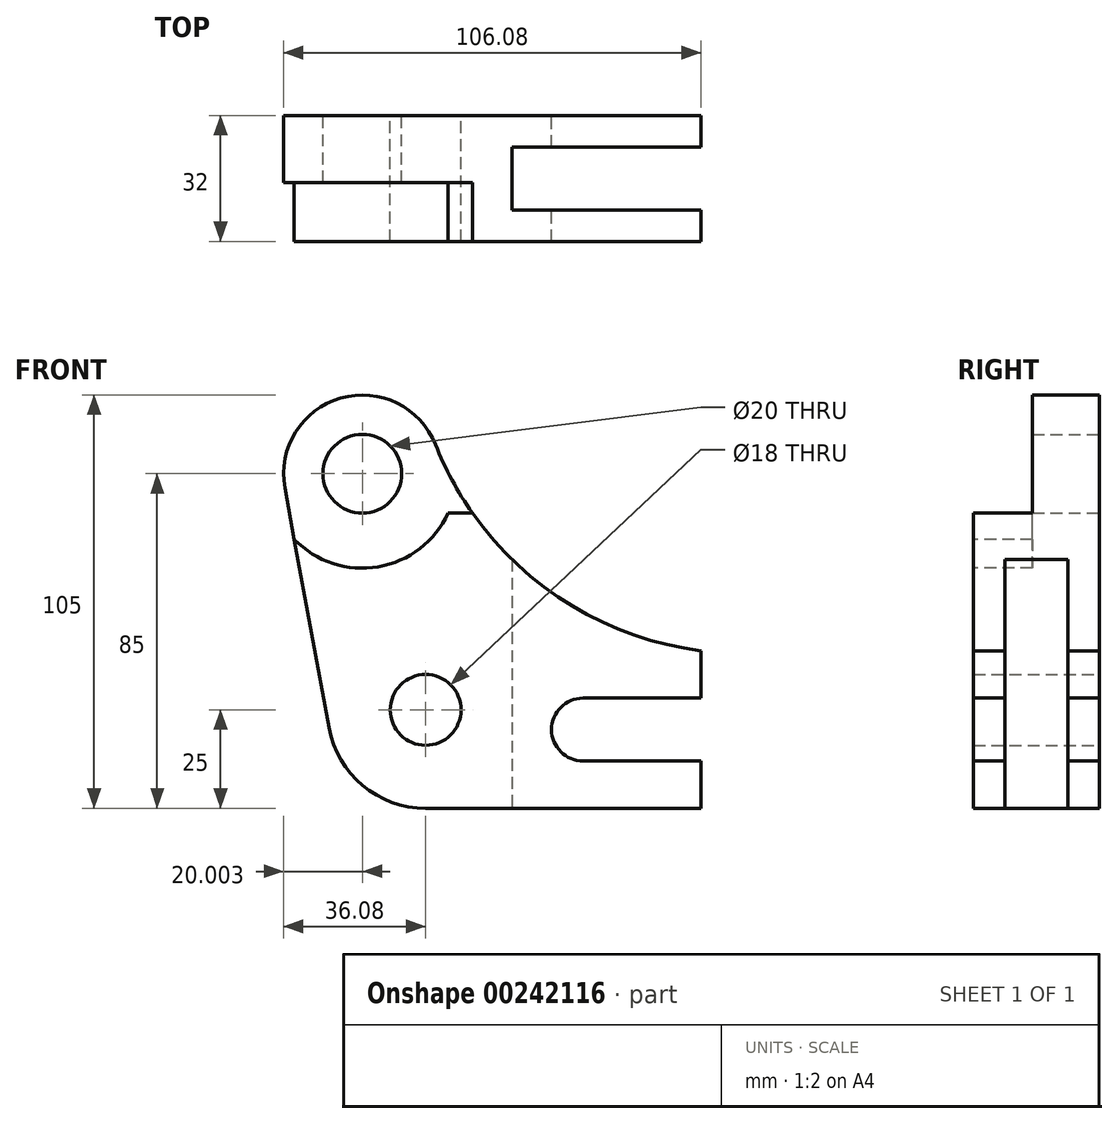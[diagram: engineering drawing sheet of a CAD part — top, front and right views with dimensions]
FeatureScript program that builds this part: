
annotation { "Feature Type Name" : "Feature", "Feature Type Description" : "" }
export const myFeature = defineFeature(function(context is Context, id is Id, definition is map)
    precondition{}
    {
        {
            var Q0;
            Q0=qCreatedBy(makeId("Front.planeOp"),FACE);
            var sketch = newSketch(context, id + "F0", { "sketchPlane" : qUnion([Q0])});
            skLineSegment(sketch, "E0", {"start": v(0, 0) * mm, "end": v(-70, 0) * mm});
            skLineSegment(sketch, "E1", {"start": v(-94.6, 20.5) * mm, "end": v(-105.75, 81.4) * mm});
            skLineSegment(sketch, "E2", {"start": v(0, 0) * mm, "end": v(0, 12) * mm});
            skLineSegment(sketch, "E3", {"start": v(0, 12) * mm, "end": v(-30, 12) * mm});
            skLineSegment(sketch, "E4", {"start": v(-30, 28) * mm, "end": v(0, 28) * mm});
            skLineSegment(sketch, "E5", {"start": v(0, 28) * mm, "end": v(0, 40) * mm});
            skArc(sketch, "E6", {"start": v(-30, 28) * mm, "mid": v(-38, 20) * mm, "end": v(-30, 12) * mm});
            skArc(sketch, "E7", {"start": v(-70, 0) * mm, "mid": v(-86, 5.8) * mm, "end": v(-94.6, 20.5) * mm});
            skArc(sketch, "E8", {"start": v(-67.48, 92.37) * mm, "mid": v(-91.6, 104.22) * mm, "end": v(-105.75, 81.4) * mm});
            skArc(sketch, "E9", {"start": v(-67.48, 92.37) * mm, "mid": v(-40.9, 56.97) * mm, "end": v(0, 40) * mm});
            skCircle(sketch, "E10", {"center": v(-70, 25) * mm, "radius": 9 * mm});
            skCircle(sketch, "E11", {"center": v(-86.08, 85) * mm, "radius": 10 * mm});
            skLineSegment(sketch, "E12", {"start": v(-58.1, 75) * mm, "end": v(-64.26, 75) * mm});
            skArc(sketch, "E13", {"start": v(-103.36, 68.35) * mm, "mid": v(-82.05, 61.34) * mm, "end": v(-64.26, 75) * mm});
            skLineSegment(sketch, "E14", {"start": v(-70, -9.53) * mm, "end": v(-70, 43.77) * mm, "construction": true});
            skLineSegment(sketch, "E15", {"start": v(-113.76, 25) * mm, "end": v(-47.36, 25) * mm, "construction": true});
            skLineSegment(sketch, "E16", {"start": v(-118.33, 85) * mm, "end": v(-31.52, 85) * mm, "construction": true});
            skLineSegment(sketch, "E17", {"start": v(-86.08, 85) * mm, "end": v(-70, 25) * mm, "construction": true});
            skSolve(sketch);
        }
        {
            var Q0;
            Q0=makeQuery(id+"F0.imprint","IMPRINT",FACE,{"disambiguationData":[TD([[makeQuery(id+"F0.imprint","IMPRINT",EDGE,{"derivedFrom":sQuery(id+"F0.wireOp",EDGE,"E0")}),-1.0]])]});
            var Q1;
            {var subQ1=sQuery(id+"F0.wireOp",EDGE,"E8");Q1=makeQuery(id+"F0.imprint","IMPRINT",FACE,{"disambiguationData":[TD([[makeQuery(id+"F0.imprint","IMPRINT",EDGE,{"derivedFrom":subQ1}),1.0]])]});}
            extrude(context, id + "F1", {"entities" : qUnion([Q0, Q1]), "depth" : 32 * mm});
        }
        {
            var Q0;
            Q0=makeQuery(id+"F1.opExtrude","CAP_FACE",FACE,{"disambiguationData":[OSD([sQuery(id+"F0.wireOp",EDGE,"E0"),sQuery(id+"F0.wireOp",EDGE,"E1"),sQuery(id+"F0.wireOp",EDGE,"E2"),sQuery(id+"F0.wireOp",EDGE,"E3"),sQuery(id+"F0.wireOp",EDGE,"E4"),sQuery(id+"F0.wireOp",EDGE,"E5"),sQuery(id+"F0.wireOp",EDGE,"E6"),sQuery(id+"F0.wireOp",EDGE,"E7"),sQuery(id+"F0.wireOp",EDGE,"E8"),sQuery(id+"F0.wireOp",EDGE,"E9"),sQuery(id+"F0.wireOp",EDGE,"E10"),sQuery(id+"F0.wireOp",EDGE,"E11")])],"isStart":false});
            var sketch = newSketch(context, id + "F2", { "sketchPlane" : qUnion([Q0])});
            skCircle(sketch, "E18.0.0", {"center": v(-86.08, 85) * mm, "radius": 10 * mm, "construction": true});
            skArc(sketch, "E19.0", {"start": v(-67.48, 92.37) * mm, "mid": v(-91.6, 104.22) * mm, "end": v(-105.75, 81.4) * mm, "construction": true});
            skArc(sketch, "E20.0", {"start": v(-103.36, 68.35) * mm, "mid": v(-82.05, 61.34) * mm, "end": v(-64.26, 75) * mm, "construction": true});
            skLineSegment(sketch, "E21.0", {"start": v(-58.1, 75) * mm, "end": v(-64.26, 75) * mm, "construction": true});
            skArc(sketch, "E22.0", {"start": v(-67.48, 92.37) * mm, "mid": v(-40.9, 56.97) * mm, "end": v(0, 40) * mm, "construction": true});
            skLineSegment(sketch, "E23.0", {"start": v(-94.6, 20.5) * mm, "end": v(-105.75, 81.4) * mm, "construction": true});
            skLineSegment(sketch, "E24", {"start": v(-86.08, 109.03) * mm, "end": v(-86.08, 56.6) * mm, "construction": true});
            skLineSegment(sketch, "E25", {"start": v(-110.8, 85) * mm, "end": v(-59, 85) * mm, "construction": true});
            skCircle(sketch, "E26", {"center": v(-86.08, 85) * mm, "radius": 10 * mm});
            skArc(sketch, "E27", {"start": v(-105.75, 81.4) * mm, "mid": v(-91.6, 104.22) * mm, "end": v(-67.48, 92.37) * mm});
            skArc(sketch, "E28", {"start": v(-64.26, 75) * mm, "mid": v(-82.05, 61.34) * mm, "end": v(-103.36, 68.35) * mm});
            skLineSegment(sketch, "E29", {"start": v(-105.75, 81.4) * mm, "end": v(-103.36, 68.35) * mm});
            skLineSegment(sketch, "E30", {"start": v(-64.26, 75) * mm, "end": v(-58.1, 75) * mm});
            skArc(sketch, "E31", {"start": v(-58.1, 75) * mm, "mid": v(-63.3, 83.4) * mm, "end": v(-67.48, 92.37) * mm});
            skSolve(sketch);
        }
        {
            var Q0;
            Q0=makeQuery(id+"F2.imprint","IMPRINT",FACE,{"disambiguationData":[TD([[makeQuery(id+"F2.imprint","IMPRINT",EDGE,{"derivedFrom":sQuery(id+"F2.wireOp",EDGE,"E26")}),-1.0]])]});
            extrude(context, id + "F3", {"entities" : qUnion([Q0]), "operationType" : NewBodyOperationType.REMOVE, "oppositeDirection" : true, "depth" : 15 * mm});
        }
        {
            var Q0;
            Q0=makeQuery(id+"F1.opExtrude","SWEPT_FACE",FACE,{"disambiguationData":[OSD([sQuery(id+"F0.wireOp",EDGE,"E0")])]});
            var sketch = newSketch(context, id + "F4", { "sketchPlane" : qUnion([Q0])});
            skLineSegment(sketch, "E32.0.0", {"start": v(-70, 0) * mm, "end": v(0, 0) * mm, "construction": true});
            skLineSegment(sketch, "E32.0.1", {"start": v(0, 0) * mm, "end": v(0, 32) * mm, "construction": true});
            skLineSegment(sketch, "E32.0.2", {"start": v(0, 32) * mm, "end": v(-70, 32) * mm, "construction": true});
            skLineSegment(sketch, "E32.0.3", {"start": v(-70, 32) * mm, "end": v(-70, 0) * mm, "construction": true});
            skLineSegment(sketch, "E33", {"start": v(0, 0) * mm, "end": v(0, 8) * mm});
            skLineSegment(sketch, "E34", {"start": v(0, 8) * mm, "end": v(-48, 8) * mm});
            skLineSegment(sketch, "E35", {"start": v(-48, 8) * mm, "end": v(-48, 24) * mm});
            skLineSegment(sketch, "E36", {"start": v(-48, 24) * mm, "end": v(0, 24) * mm});
            skLineSegment(sketch, "E37", {"start": v(0, 24) * mm, "end": v(0, 8) * mm});
            skPoint(sketch, "E38", {"position": v(0, 16) * mm});
            skSolve(sketch);
        }
        {
            var Q0;
            Q0=makeQuery(id+"F4.imprint","IMPRINT",FACE,{"disambiguationData":[TD([[makeQuery(id+"F4.imprint","IMPRINT",EDGE,{"derivedFrom":sQuery(id+"F4.wireOp",EDGE,"E34")}),-1.0]])]});
            extrude(context, id + "F5", {"entities" : qUnion([Q0]), "operationType" : NewBodyOperationType.REMOVE, "endBound" : BoundingType.THROUGH_ALL, "oppositeDirection" : true, "depth" : 25 * mm});
        }
    });
